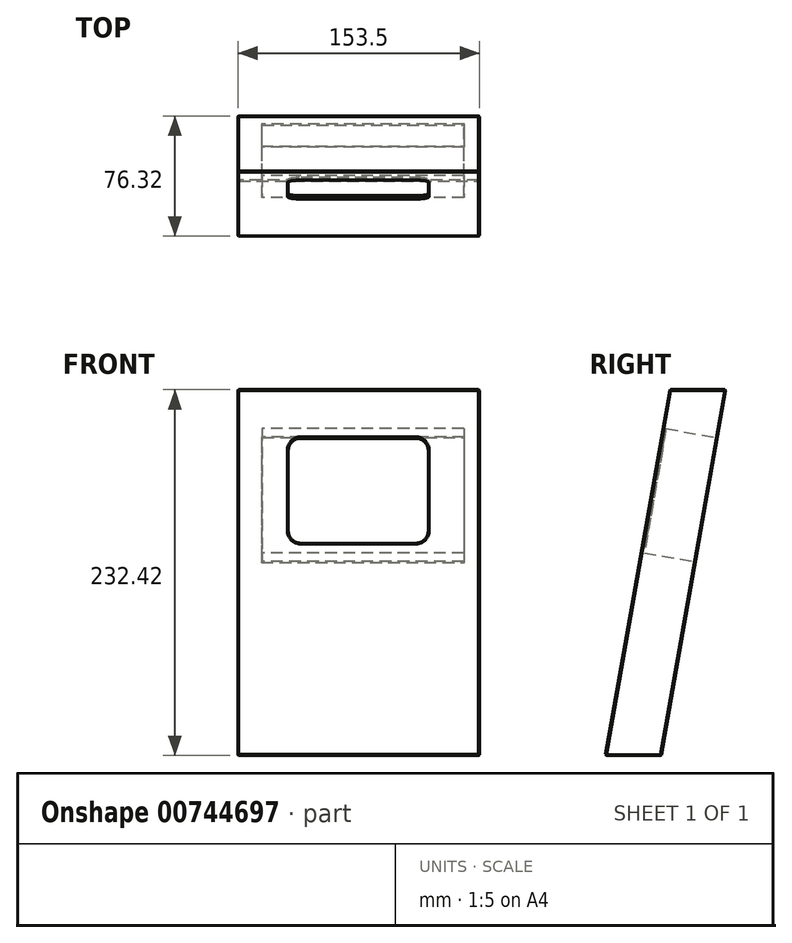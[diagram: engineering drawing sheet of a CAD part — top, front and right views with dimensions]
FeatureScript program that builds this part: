
annotation { "Feature Type Name" : "Feature", "Feature Type Description" : "" }
export const myFeature = defineFeature(function(context is Context, id is Id, definition is map)
    precondition{}
    {
        {
            var Q0;
            Q0=qCreatedBy(makeId("Right.planeOp"),FACE);
            var sketch = newSketch(context, id + "F0", { "sketchPlane" : qUnion([Q0])});
            skLineSegment(sketch, "E0", {"start": v(44.6, 87.86) * mm, "end": v(80.14, 87.86) * mm});
            skLineSegment(sketch, "E1", {"start": v(80.14, 87.86) * mm, "end": v(39.16, -144.56) * mm});
            skLineSegment(sketch, "E2", {"start": v(39.16, -144.56) * mm, "end": v(3.62, -144.56) * mm});
            skLineSegment(sketch, "E3", {"start": v(3.62, -144.56) * mm, "end": v(44.6, 87.86) * mm});
            skSolve(sketch);
        }
        {
            var Q0;
            Q0=qSketchRegion(id+"F0",true);
            var Q1;
            Q1=qSketchRegion(id+"F2",true);
            extrude(context, id + "F1", {"entities" : qUnion([Q0, Q1]), "oppositeDirection" : true, "depth" : 153.5 * mm, "offsetDistance" : 25 * mm});
        }
        {
            var Q0;
            Q0=makeQuery(id+"F1.opExtrude","SWEPT_FACE",FACE,{"disambiguationData":[OSD([sQuery(id+"F0.wireOp",EDGE,"E3")])]});
            var sketch = newSketch(context, id + "F2", { "sketchPlane" : qUnion([Q0])});
            skLineSegment(sketch, "E4.bottom", {"start": v(-113.5, 63.27) * mm, "end": v(-40.5, 63.27) * mm});
            skLineSegment(sketch, "E4.top", {"start": v(-113.5, -4.73) * mm, "end": v(-40.5, -4.73) * mm});
            skLineSegment(sketch, "E4.left", {"start": v(-121.5, 55.27) * mm, "end": v(-121.5, 3.27) * mm});
            skLineSegment(sketch, "E4.right", {"start": v(-32.5, 55.27) * mm, "end": v(-32.5, 3.27) * mm});
            skPoint(sketch, "E5.visualSharp", {"position": v(-32.5, 63.27) * mm});
            skArc(sketch, "E5.filletArc", {"start": v(-32.5, 55.27) * mm, "mid": v(-34.84, 60.92) * mm, "end": v(-40.5, 63.27) * mm});
            skPoint(sketch, "E6.visualSharp", {"position": v(-121.5, 63.27) * mm});
            skArc(sketch, "E6.filletArc", {"start": v(-113.5, 63.27) * mm, "mid": v(-119.16, 60.92) * mm, "end": v(-121.5, 55.27) * mm});
            skPoint(sketch, "E7.visualSharp", {"position": v(-121.5, -4.73) * mm});
            skArc(sketch, "E7.filletArc", {"start": v(-121.5, 3.27) * mm, "mid": v(-119.16, -2.4) * mm, "end": v(-113.5, -4.73) * mm});
            skPoint(sketch, "E8.visualSharp", {"position": v(-32.5, -4.73) * mm});
            skArc(sketch, "E8.filletArc", {"start": v(-40.5, -4.73) * mm, "mid": v(-34.84, -2.4) * mm, "end": v(-32.5, 3.27) * mm});
            skSolve(sketch);
        }
        {
            var Q0;
            Q0=makeQuery(id+"F2.imprint","IMPRINT",FACE,{"disambiguationData":[TD([[makeQuery(id+"F2.imprint","IMPRINT",EDGE,{"derivedFrom":sQuery(id+"F2.wireOp",EDGE,"E4.bottom")}),-1.0]])]});
            extrude(context, id + "F3", {"entities" : qUnion([Q0]), "operationType" : NewBodyOperationType.REMOVE, "endBound" : BoundingType.THROUGH_ALL, "oppositeDirection" : true, "depth" : 25 * mm, "offsetDistance" : 25 * mm});
        }
        {
            var Q0;
            Q0=makeQuery(id+"F1.opExtrude","SWEPT_FACE",FACE,{"disambiguationData":[OSD([sQuery(id+"F0.wireOp",EDGE,"E1")])]});
            var sketch = newSketch(context, id + "F4", { "sketchPlane" : qUnion([Q0])});
            skLineSegment(sketch, "E9.bottom", {"start": v(10, 69.44) * mm, "end": v(138, 69.44) * mm});
            skLineSegment(sketch, "E9.top", {"start": v(10, -10.56) * mm, "end": v(138, -10.56) * mm});
            skLineSegment(sketch, "E9.left", {"start": v(10, 69.44) * mm, "end": v(10, -10.56) * mm});
            skLineSegment(sketch, "E9.right", {"start": v(138, 69.44) * mm, "end": v(138, -10.56) * mm});
            skSolve(sketch);
        }
        {
            var Q0;
            Q0=qSketchRegion(id+"F4",true);
            extrude(context, id + "F5", {"entities" : qUnion([Q0]), "operationType" : NewBodyOperationType.REMOVE, "oppositeDirection" : true, "depth" : 33 * mm, "offsetDistance" : 25 * mm});
        }
        {
            var Q0;
            Q0=makeQuery(id+"F1.opExtrude","SWEPT_FACE",FACE,{"disambiguationData":[OSD([sQuery(id+"F0.wireOp",EDGE,"E3")])]});
            var Q1;
            Q1=makeQuery(id+"F1.opExtrude","CAP_FACE",FACE,{"disambiguationData":[OSD([sQuery(id+"F0.wireOp",EDGE,"E0"),sQuery(id+"F0.wireOp",EDGE,"E1"),sQuery(id+"F0.wireOp",EDGE,"E2"),sQuery(id+"F0.wireOp",EDGE,"E3")])],"isStart":true});
            var Q2;
            Q2=makeQuery(id+"F1.opExtrude","SWEPT_FACE",FACE,{"disambiguationData":[OSD([sQuery(id+"F0.wireOp",EDGE,"E0")])]});
            var Q3;
            Q3=makeQuery(id+"F1.opExtrude","CAP_FACE",FACE,{"disambiguationData":[OSD([sQuery(id+"F0.wireOp",EDGE,"E0"),sQuery(id+"F0.wireOp",EDGE,"E1"),sQuery(id+"F0.wireOp",EDGE,"E2"),sQuery(id+"F0.wireOp",EDGE,"E3")])],"isStart":false});
            var Q4;
            Q4=makeQuery(id+"F1.opExtrude","SWEPT_FACE",FACE,{"disambiguationData":[OSD([sQuery(id+"F0.wireOp",EDGE,"E1")])]});
            chamfer(context, id + "F6", {"entities" : qUnion([Q0, Q1, Q2, Q3, Q4]), "width" : 0.5 * mm, "tangentPropagation" : true});
        }
    });
